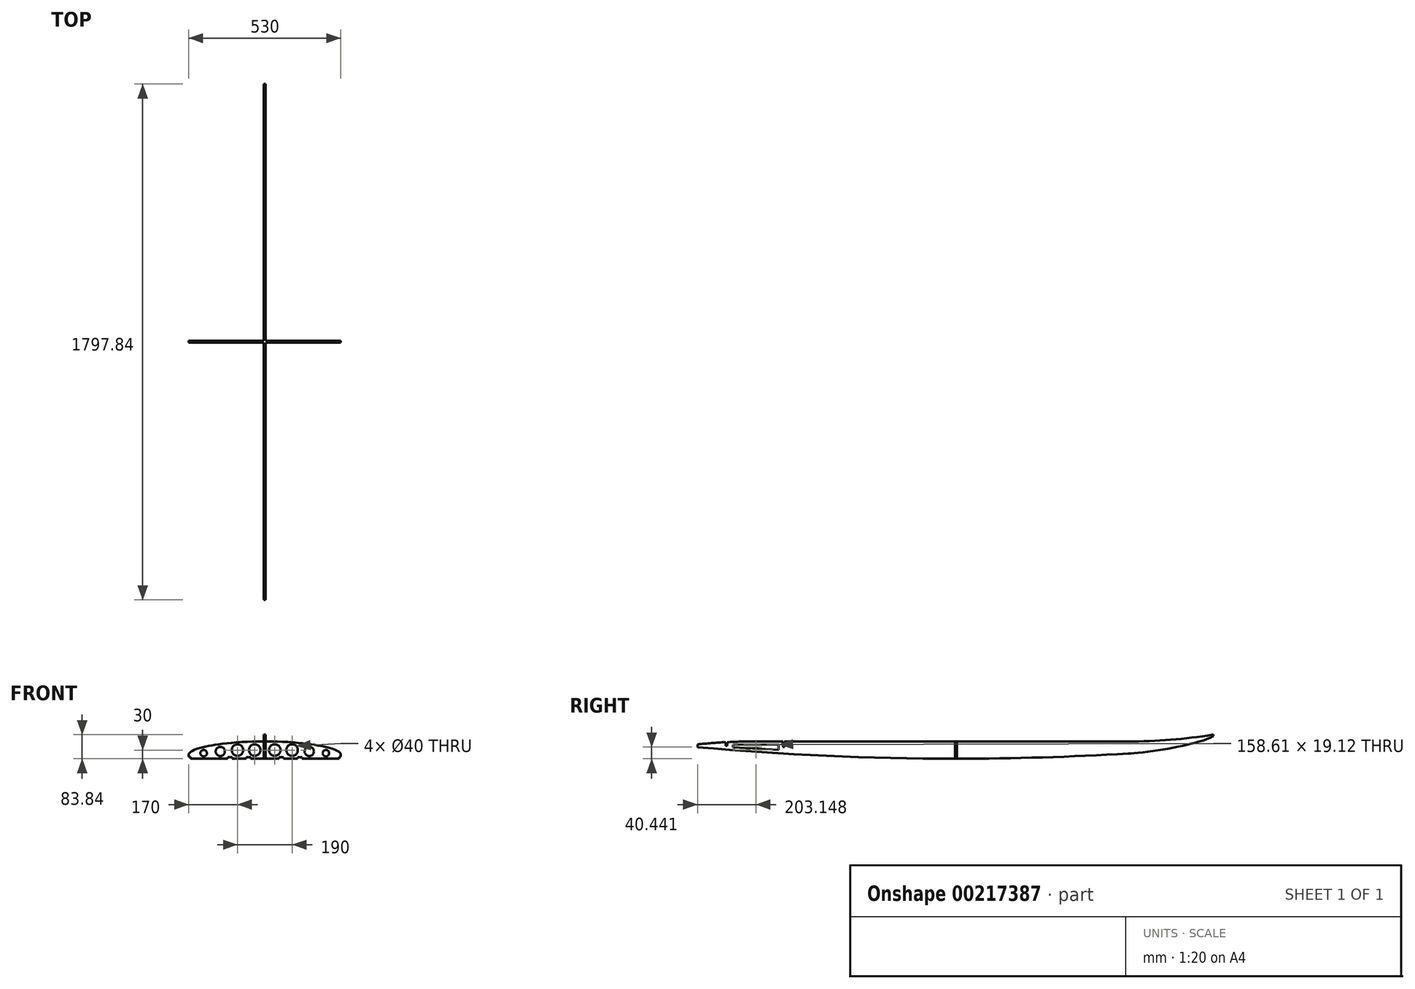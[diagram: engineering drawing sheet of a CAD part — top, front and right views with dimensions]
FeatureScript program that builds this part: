
annotation { "Feature Type Name" : "Feature", "Feature Type Description" : "" }
export const myFeature = defineFeature(function(context is Context, id is Id, definition is map)
    precondition{}
    {
        {
            var Q0;
            Q0=qCreatedBy(makeId("Top.planeOp"),FACE);
            var sketch = newSketch(context, id + "F0", { "sketchPlane" : qUnion([Q0])});
            skLineSegment(sketch, "E0", {"start": v(80, 0) * mm, "end": v(270, 0) * mm, "construction": true});
            skLineSegment(sketch, "E1", {"start": v(270, 0) * mm, "end": v(270, 1800) * mm, "construction": true});
            skLineSegment(sketch, "E2", {"start": v(270, 1800) * mm, "end": v(0, 1800) * mm, "construction": true});
            skLineSegment(sketch, "E3", {"start": v(0, 1800) * mm, "end": v(0, 0) * mm, "construction": true});
            skLineSegment(sketch, "E4", {"start": v(0, 900) * mm, "end": v(270, 900) * mm, "construction": true});
            skFitSpline(sketch, "E5", {"points": [v(0, 1800) * mm, v(270, 900) * mm], "startDerivative": vector(859.7, 0) * mm, "endDerivative": vector(0, -984.96) * mm});
            skLineSegment(sketch, "E6", {"start": v(180, 0) * mm, "end": v(80, 0) * mm});
            skFitSpline(sketch, "E7", {"points": [v(270, 900) * mm, v(180, 0) * mm], "startDerivative": vector(0, -917.27) * mm, "endDerivative": vector(-160.43, -517.36) * mm});
            skFitSpline(sketch, "E8.MirrorCS", {"points": [v(0, 1800) * mm, v(-270, 900) * mm], "startDerivative": vector(-859.7, 0) * mm, "endDerivative": vector(0, -984.96) * mm});
            skFitSpline(sketch, "E9.MirrorCS", {"points": [v(-270, 900) * mm, v(-180, 0) * mm], "startDerivative": vector(0, -917.27) * mm, "endDerivative": vector(160.43, -517.36) * mm});
            skLineSegment(sketch, "E10.MirrorCS", {"start": v(-180, 0) * mm, "end": v(-80, 0) * mm});
            skLineSegment(sketch, "E11", {"start": v(0, 40) * mm, "end": v(80, 0) * mm});
            skLineSegment(sketch, "E12.MirrorCS", {"start": v(0, 40) * mm, "end": v(-80, 0) * mm});
            skPoint(sketch, "E13.orphan", {"position": v(0, 0) * mm});
            skSolve(sketch);
        }
        {
            var Q0;
            Q0=qCreatedBy(makeId("Right.planeOp"),FACE);
            var sketch = newSketch(context, id + "F1", { "sketchPlane" : qUnion([Q0])});
            skLineSegment(sketch, "E14", {"start": v(0, 40) * mm, "end": v(0, 0) * mm, "construction": true});
            skLineSegment(sketch, "E15", {"start": v(0, 0) * mm, "end": v(1800, 0) * mm, "construction": true});
            skLineSegment(sketch, "E16", {"start": v(1800, 0) * mm, "end": v(1800, 80) * mm, "construction": true});
            skLineSegment(sketch, "E17", {"start": v(1300, 0) * mm, "end": v(1300, 7.89) * mm, "construction": true});
            skPoint(sketch, "E18", {"position": v(900, 0) * mm});
            skArc(sketch, "E19", {"start": v(0, 40) * mm, "mid": v(649.48, 3.1) * mm, "end": v(1300, 7.89) * mm});
            skFitSpline(sketch, "E20", {"points": [v(1300, 7.89) * mm, v(1800, 80) * mm], "startDerivative": vector(937.16, 36.98) * mm, "endDerivative": vector(218.5, 99.34) * mm});
            skLineSegment(sketch, "E21", {"start": v(0, 70) * mm, "end": v(1657.6, 70) * mm, "construction": true});
            skLineSegment(sketch, "E22", {"start": v(200, 0) * mm, "end": v(200, 70) * mm, "construction": true});
            skLineSegment(sketch, "E23", {"start": v(0, 40) * mm, "end": v(0, 60) * mm});
            skArc(sketch, "E24", {"start": v(200, 70) * mm, "mid": v(99.88, 67.5) * mm, "end": v(0, 60) * mm});
            skLineSegment(sketch, "E25", {"start": v(1800, 80) * mm, "end": v(1793.55, 93.54) * mm});
            skLineSegment(sketch, "E26", {"start": v(1300, 7.89) * mm, "end": v(1300, 70) * mm, "construction": true});
            skArc(sketch, "E27", {"start": v(1300, 70) * mm, "mid": v(1547.06, 75.89) * mm, "end": v(1793.55, 93.54) * mm});
            skLineSegment(sketch, "E28", {"start": v(200, 70) * mm, "end": v(1300, 70) * mm});
            skSolve(sketch);
        }
        {
            var Q0;
            Q0=qCreatedBy(makeId("Front.planeOp"),FACE);
            var Q1;
            Q1=sQuery(id+"F1.wireOp",VERTEX,"E18");
            cPlane(context, id + "F2", {"entities" : qUnion([Q0, Q1]), "cplaneType" : CPlaneType.PLANE_POINT, "offset" : 25 * mm, "width" : 150 * mm, "height" : 150 * mm});
        }
        {
            var Q0;
            Q0=qCreatedBy(id+"F2.planeOp",FACE);
            var sketch = newSketch(context, id + "F3", { "sketchPlane" : qUnion([Q0])});
            skLineSegment(sketch, "E29", {"start": v(0, 0) * mm, "end": v(-260, 0) * mm});
            skLineSegment(sketch, "E30", {"start": v(0, 70) * mm, "end": v(-270, 70) * mm, "construction": true});
            skLineSegment(sketch, "E31", {"start": v(0, 0) * mm, "end": v(0, 70) * mm});
            skLineSegment(sketch, "E32", {"start": v(-270, 0) * mm, "end": v(-270, 80.9) * mm, "construction": true});
            skPoint(sketch, "E33", {"position": v(-270, 20) * mm});
            skFitSpline(sketch, "E34", {"points": [v(-270, 20) * mm, v(0, 70) * mm], "startDerivative": vector(0, 90) * mm, "endDerivative": vector(405, 0) * mm});
            skLineSegment(sketch, "E35", {"start": v(-270, 20) * mm, "end": v(-270, 14) * mm});
            skArc(sketch, "E36", {"start": v(-270, 14) * mm, "mid": v(-267.24, 5.4) * mm, "end": v(-260, 0) * mm});
            skSolve(sketch);
        }
        {
            var Q0;
            Q0=qCreatedBy(makeId("Front.planeOp"),FACE);
            cPlane(context, id + "F4", {"entities" : qUnion([Q0]), "cplaneType" : CPlaneType.OFFSET, "offset" : 700 * mm, "oppositeDirection" : true, "width" : 150 * mm, "height" : 150 * mm});
        }
        {
            var Q0;
            Q0=qCreatedBy(makeId("Front.planeOp"),FACE);
            cPlane(context, id + "F5", {"entities" : qUnion([Q0]), "cplaneType" : CPlaneType.OFFSET, "offset" : 500 * mm, "oppositeDirection" : true, "width" : 150 * mm, "height" : 150 * mm});
        }
        {
            var Q0;
            Q0=qCreatedBy(makeId("Front.planeOp"),FACE);
            cPlane(context, id + "F6", {"entities" : qUnion([Q0]), "cplaneType" : CPlaneType.OFFSET, "offset" : 300 * mm, "oppositeDirection" : true, "width" : 150 * mm, "height" : 150 * mm});
        }
        {
            var Q0;
            Q0=qCreatedBy(makeId("Front.planeOp"),FACE);
            cPlane(context, id + "F7", {"entities" : qUnion([Q0]), "cplaneType" : CPlaneType.OFFSET, "offset" : 100 * mm, "oppositeDirection" : true, "width" : 150 * mm, "height" : 150 * mm});
        }
        {
            var Q0;
            Q0=qCreatedBy(makeId("Front.planeOp"),FACE);
            cPlane(context, id + "F8", {"entities" : qUnion([Q0]), "cplaneType" : CPlaneType.OFFSET, "offset" : 1100 * mm, "oppositeDirection" : true, "width" : 150 * mm, "height" : 150 * mm});
        }
        {
            var Q0;
            Q0=qCreatedBy(makeId("Front.planeOp"),FACE);
            cPlane(context, id + "F9", {"entities" : qUnion([Q0]), "cplaneType" : CPlaneType.OFFSET, "offset" : 1300 * mm, "oppositeDirection" : true, "width" : 150 * mm, "height" : 150 * mm});
        }
        {
            var Q0;
            Q0=qCreatedBy(makeId("Front.planeOp"),FACE);
            cPlane(context, id + "F10", {"entities" : qUnion([Q0]), "cplaneType" : CPlaneType.OFFSET, "offset" : 1500 * mm, "oppositeDirection" : true, "width" : 150 * mm, "height" : 150 * mm});
        }
        {
            var Q0;
            Q0=qCreatedBy(makeId("Front.planeOp"),FACE);
            cPlane(context, id + "F11", {"entities" : qUnion([Q0]), "cplaneType" : CPlaneType.OFFSET, "offset" : 1700 * mm, "oppositeDirection" : true, "width" : 150 * mm, "height" : 150 * mm});
        }
        {
            var Q0;
            Q0=qCreatedBy(id+"F11.planeOp",FACE);
            var sketch = newSketch(context, id + "F12", { "sketchPlane" : qUnion([Q0])});
            skLineSegment(sketch, "E37", {"start": v(0, 47.61) * mm, "end": v(0, 85.45) * mm});
            skLineSegment(sketch, "E38", {"start": v(166.66, 0) * mm, "end": v(-166.66, 0) * mm, "construction": true});
            skLineSegment(sketch, "E39", {"start": v(-166.66, 0) * mm, "end": v(-166.66, 85.45) * mm, "construction": true});
            skLineSegment(sketch, "E40", {"start": v(-166.66, 85.45) * mm, "end": v(0, 85.45) * mm, "construction": true});
            skLineSegment(sketch, "E41", {"start": v(0, 47.61) * mm, "end": v(-166.66, 47.61) * mm, "construction": true});
            skLineSegment(sketch, "E42", {"start": v(0, 47.61) * mm, "end": v(-159.96, 47.61) * mm});
            skLineSegment(sketch, "E43", {"start": v(-166.66, 54.31) * mm, "end": v(-166.66, 57.18) * mm});
            skArc(sketch, "E44", {"start": v(-166.66, 54.31) * mm, "mid": v(-164.7, 49.57) * mm, "end": v(-159.96, 47.61) * mm});
            skFitSpline(sketch, "E45", {"points": [v(-166.66, 57.18) * mm, v(0, 85.45) * mm], "startDerivative": vector(0, 43.07) * mm, "endDerivative": vector(249.99, 0) * mm});
            skSolve(sketch);
        }
        {
            var Q0;
            Q0=qCreatedBy(id+"F2.planeOp",FACE);
            var sketch = newSketch(context, id + "F13", { "sketchPlane" : qUnion([Q0])});
            skLineSegment(sketch, "E46.0.0", {"start": v(-270, 20) * mm, "end": v(-270, 14) * mm, "construction": true});
            skArc(sketch, "E46.0.1", {"start": v(-270, 14) * mm, "mid": v(-267.24, 5.4) * mm, "end": v(-260, 0) * mm, "construction": true});
            skLineSegment(sketch, "E46.0.2", {"start": v(-260, 0) * mm, "end": v(0, 0) * mm, "construction": true});
            skLineSegment(sketch, "E46.0.3", {"start": v(0, 0) * mm, "end": v(0, 70) * mm, "construction": true});
            skFitSpline(sketch, "E46.0.4", {"points": [v(0, 70) * mm, v(-135, 70) * mm, v(-270, 50) * mm, v(-270, 20) * mm], "construction": true});
            skLineSegment(sketch, "E47.0", {"start": v(-265, 20) * mm, "end": v(-265, 14) * mm});
            skFitSpline(sketch, "E47.1", {"points": [v(0, 65) * mm, v(-16.81, 65) * mm, v(-50.44, 64.38) * mm, v(-99.3, 61.7) * mm, v(-137.36, 58.1) * mm, v(-165.4, 54.46) * mm, v(-185.04, 51.38) * mm, v(-203.06, 47.96) * mm, v(-219.26, 44.2) * mm, v(-233.42, 40.17) * mm, v(-245.31, 35.88) * mm, v(-253.1, 32.15) * mm, v(-257.93, 29.16) * mm, v(-260.8, 26.96) * mm, v(-262.89, 24.87) * mm, v(-264.22, 22.98) * mm, v(-264.88, 21.38) * mm, v(-265, 20.47) * mm, v(-265, 20) * mm]});
            skLineSegment(sketch, "E48", {"start": v(-3, 5) * mm, "end": v(-49.5, 5) * mm});
            skLineSegment(sketch, "E49", {"start": v(-265, 14) * mm, "end": v(-265, 11) * mm});
            skLineSegment(sketch, "E50", {"start": v(-265, 11) * mm, "end": v(-259, 11) * mm});
            skLineSegment(sketch, "E51", {"start": v(-259, 11) * mm, "end": v(-259, 5) * mm});
            skLineSegment(sketch, "E52.MirrorCS", {"start": v(3, 5) * mm, "end": v(49.5, 5) * mm});
            skLineSegment(sketch, "E53.MirrorCS", {"start": v(259, 11) * mm, "end": v(259, 5) * mm});
            skLineSegment(sketch, "E54.MirrorCS", {"start": v(265, 11) * mm, "end": v(259, 11) * mm});
            skLineSegment(sketch, "E55.MirrorCS", {"start": v(265, 14) * mm, "end": v(265, 11) * mm});
            skLineSegment(sketch, "E56.MirrorCS", {"start": v(265, 20) * mm, "end": v(265, 14) * mm});
            skFitSpline(sketch, "E57.MirrorCS", {"points": [v(0, 70) * mm, v(135, 70) * mm, v(270, 50) * mm, v(270, 20) * mm], "construction": true});
            skFitSpline(sketch, "E58.0", {"points": [v(0, 65) * mm, v(16.81, 65) * mm, v(50.44, 64.38) * mm, v(99.3, 61.7) * mm, v(137.36, 58.1) * mm, v(165.4, 54.46) * mm, v(185.04, 51.38) * mm, v(203.06, 47.96) * mm, v(219.26, 44.2) * mm, v(233.42, 40.17) * mm, v(245.31, 35.88) * mm, v(253.1, 32.15) * mm, v(257.93, 29.16) * mm, v(260.8, 26.96) * mm, v(262.89, 24.87) * mm, v(264.22, 22.98) * mm, v(264.88, 21.38) * mm, v(265, 20.47) * mm, v(265, 20) * mm]});
            skCircle(sketch, "E59", {"center": v(-35, 35) * mm, "radius": 20 * mm});
            skPoint(sketch, "E59.first.point", {"position": v(-54.92, 33.24) * mm});
            skPoint(sketch, "E59.second.point", {"position": v(-26.96, 16.69) * mm});
            skPoint(sketch, "E59.third.point", {"position": v(-42.78, 16.57) * mm});
            skCircle(sketch, "E60.1.0.0", {"center": v(-95, 35) * mm, "radius": 20 * mm});
            skLineSegment(sketch, "E60.direction1", {"start": v(-35, 35) * mm, "end": v(-95, 35) * mm, "construction": true});
            skCircle(sketch, "E61", {"center": v(-154.99, 30.03) * mm, "radius": 16.06 * mm});
            skCircle(sketch, "E62", {"center": v(-212.9, 24.16) * mm, "radius": 11.32 * mm});
            skCircle(sketch, "E63.MirrorC", {"center": v(35, 35) * mm, "radius": 20 * mm});
            skCircle(sketch, "E64.MirrorC", {"center": v(95, 35) * mm, "radius": 20 * mm});
            skCircle(sketch, "E65.MirrorC", {"center": v(154.99, 30.03) * mm, "radius": 16.06 * mm});
            skCircle(sketch, "E66.MirrorC", {"center": v(212.9, 24.16) * mm, "radius": 11.32 * mm});
            skLineSegment(sketch, "E67.top", {"start": v(-64.5, 10) * mm, "end": v(-49.5, 10) * mm});
            skLineSegment(sketch, "E67.left", {"start": v(-64.5, 5) * mm, "end": v(-64.5, 10) * mm});
            skLineSegment(sketch, "E67.right", {"start": v(-49.5, 5) * mm, "end": v(-49.5, 10) * mm});
            skLineSegment(sketch, "E68.top", {"start": v(-129.5, 10) * mm, "end": v(-114.5, 10) * mm});
            skLineSegment(sketch, "E68.left", {"start": v(-129.5, 5) * mm, "end": v(-129.5, 10) * mm});
            skLineSegment(sketch, "E68.right", {"start": v(-114.5, 5) * mm, "end": v(-114.5, 10) * mm});
            skLineSegment(sketch, "E69.trimOffspring", {"start": v(-129.5, 5) * mm, "end": v(-259, 5) * mm});
            skLineSegment(sketch, "E70.trimOffspring", {"start": v(-64.5, 5) * mm, "end": v(-114.5, 5) * mm});
            skLineSegment(sketch, "E71", {"start": v(-3, 5) * mm, "end": v(-3, 35) * mm});
            skLineSegment(sketch, "E72", {"start": v(-3, 35) * mm, "end": v(0, 35) * mm});
            skLineSegment(sketch, "E73.MirrorCS", {"start": v(129.5, 5) * mm, "end": v(129.5, 10) * mm});
            skLineSegment(sketch, "E74.MirrorCS", {"start": v(129.5, 10) * mm, "end": v(114.5, 10) * mm});
            skLineSegment(sketch, "E75.MirrorCS", {"start": v(114.5, 5) * mm, "end": v(114.5, 10) * mm});
            skLineSegment(sketch, "E76.MirrorCS", {"start": v(64.5, 5) * mm, "end": v(64.5, 10) * mm});
            skLineSegment(sketch, "E77.MirrorCS", {"start": v(64.5, 10) * mm, "end": v(49.5, 10) * mm});
            skLineSegment(sketch, "E78.MirrorCS", {"start": v(49.5, 5) * mm, "end": v(49.5, 10) * mm});
            skLineSegment(sketch, "E79.MirrorCS", {"start": v(3, 5) * mm, "end": v(3, 35) * mm});
            skLineSegment(sketch, "E80.MirrorCS", {"start": v(3, 35) * mm, "end": v(0, 35) * mm});
            skPoint(sketch, "E81.orphan", {"position": v(0, 5) * mm});
            skLineSegment(sketch, "E82.trimOffspring", {"start": v(129.5, 5) * mm, "end": v(259, 5) * mm});
            skLineSegment(sketch, "E83.trimOffspring", {"start": v(64.5, 5) * mm, "end": v(114.5, 5) * mm});
            skSolve(sketch);
        }
        {
            var Q0;
            Q0 = qSketchRegion(id + "F13", true);
            extrude(context, id + "F14", {"entities" : qUnion([Q0]), "endBound" : BoundingType.SYMMETRIC, "depth" : 6 * mm});
        }
        {
            var Q0;
            Q0=qCreatedBy(makeId("Right.planeOp"),FACE);
            var sketch = newSketch(context, id + "F15", { "sketchPlane" : qUnion([Q0])});
            skLineSegment(sketch, "E84.0.0", {"start": v(1300, 70) * mm, "end": v(200, 70) * mm, "construction": true});
            skArc(sketch, "E84.0.1", {"start": v(200, 70) * mm, "mid": v(99.88, 67.5) * mm, "end": v(0, 60) * mm, "construction": true});
            skLineSegment(sketch, "E84.0.2", {"start": v(0, 54.97) * mm, "end": v(0, 45.02) * mm});
            skArc(sketch, "E84.0.3", {"start": v(0, 40) * mm, "mid": v(649.48, 3.1) * mm, "end": v(1300, 7.89) * mm, "construction": true});
            skFitSpline(sketch, "E84.0.4", {"points": [v(1500, 17.76) * mm, v(1604.32, 23.94) * mm, v(1764.69, 55.9) * mm, v(1800, 80) * mm], "construction": true});
            skLineSegment(sketch, "E84.0.5", {"start": v(1797.84, 84.54) * mm, "end": v(1795.79, 88.84) * mm});
            skArc(sketch, "E84.0.6", {"start": v(1793.55, 93.54) * mm, "mid": v(1547.06, 75.89) * mm, "end": v(1300, 70) * mm, "construction": true});
            skFitSpline(sketch, "E85.0", {"points": [v(1499.7, 22.75) * mm, v(1512.66, 23.52) * mm, v(1540.34, 25.85) * mm, v(1585.06, 31.38) * mm, v(1630.8, 38.53) * mm, v(1675.42, 46.92) * mm, v(1709.9, 54.6) * mm, v(1734.76, 60.95) * mm, v(1751.78, 65.76) * mm, v(1766.9, 70.58) * mm, v(1779.8, 75.32) * mm, v(1788.48, 79.16) * mm, v(1793.98, 82.08) * mm, v(1796.2, 83.46) * mm, v(1797.18, 84.13) * mm]});
            skArc(sketch, "E85.1", {"start": v(0.44, 44.98) * mm, "mid": v(749.66, 6.11) * mm, "end": v(1499.7, 22.75) * mm});
            skArc(sketch, "E86.0", {"start": v(200, 65) * mm, "mid": v(151.3, 64.4) * mm, "end": v(102.63, 62.63) * mm});
            skLineSegment(sketch, "E86.1", {"start": v(1500, 65) * mm, "end": v(302.77, 65) * mm});
            skArc(sketch, "E86.2", {"start": v(1794.35, 88.6) * mm, "mid": v(1647.65, 70.91) * mm, "end": v(1500, 65) * mm});
            skLineSegment(sketch, "E87", {"start": v(0.5, 55.02) * mm, "end": v(0, 54.97) * mm});
            skLineSegment(sketch, "E88", {"start": v(0.44, 44.98) * mm, "end": v(0, 45.02) * mm});
            skLineSegment(sketch, "E89", {"start": v(1794.35, 88.6) * mm, "end": v(1795.79, 88.84) * mm});
            skLineSegment(sketch, "E90", {"start": v(1797.18, 84.13) * mm, "end": v(1797.84, 84.54) * mm});
            skLineSegment(sketch, "E91", {"start": v(102.63, 62.63) * mm, "end": v(102.63, 50.1) * mm});
            skLineSegment(sketch, "E92", {"start": v(102.63, 50.1) * mm, "end": v(97.93, 50.1) * mm});
            skLineSegment(sketch, "E93", {"start": v(97.93, 50.1) * mm, "end": v(97.93, 62.4) * mm});
            skArc(sketch, "E94.trimOffspring", {"start": v(97.93, 62.4) * mm, "mid": v(49.17, 59.3) * mm, "end": v(0.5, 55.02) * mm});
            skLineSegment(sketch, "E95.top", {"start": v(297.32, 45.73) * mm, "end": v(302.77, 45.73) * mm});
            skLineSegment(sketch, "E95.left", {"start": v(297.32, 65) * mm, "end": v(297.32, 45.73) * mm});
            skLineSegment(sketch, "E95.right", {"start": v(302.77, 65) * mm, "end": v(302.77, 45.73) * mm});
            skLineSegment(sketch, "E96.trimOffspring", {"start": v(297.32, 65) * mm, "end": v(200, 65) * mm});
            skArc(sketch, "E97.0", {"start": v(1.33, 54.94) * mm, "mid": v(749.81, 16.11) * mm, "end": v(1499.11, 32.73) * mm, "construction": true});
            skArc(sketch, "E98.0", {"start": v(200, 55) * mm, "mid": v(151.55, 54.41) * mm, "end": v(103.12, 52.64) * mm, "construction": true});
            skLineSegment(sketch, "E98.1", {"start": v(297.32, 55) * mm, "end": v(200, 55) * mm, "construction": true});
            skLineSegment(sketch, "E99", {"start": v(123.84, 44.78) * mm, "end": v(123.84, 53.54) * mm});
            skLineSegment(sketch, "E100", {"start": v(123.84, 53.54) * mm, "end": v(282.45, 55) * mm});
            skLineSegment(sketch, "E101", {"start": v(282.45, 55) * mm, "end": v(282.45, 35.88) * mm});
            skLineSegment(sketch, "E102", {"start": v(282.45, 35.88) * mm, "end": v(123.84, 44.78) * mm});
            skSolve(sketch);
        }
        {
            var Q0;
            Q0 = qSketchRegion(id + "F15", true);
            extrude(context, id + "F16", {"entities" : qUnion([Q0]), "operationType" : NewBodyOperationType.ADD, "endBound" : BoundingType.SYMMETRIC, "depth" : 6 * mm});
        }
    });
